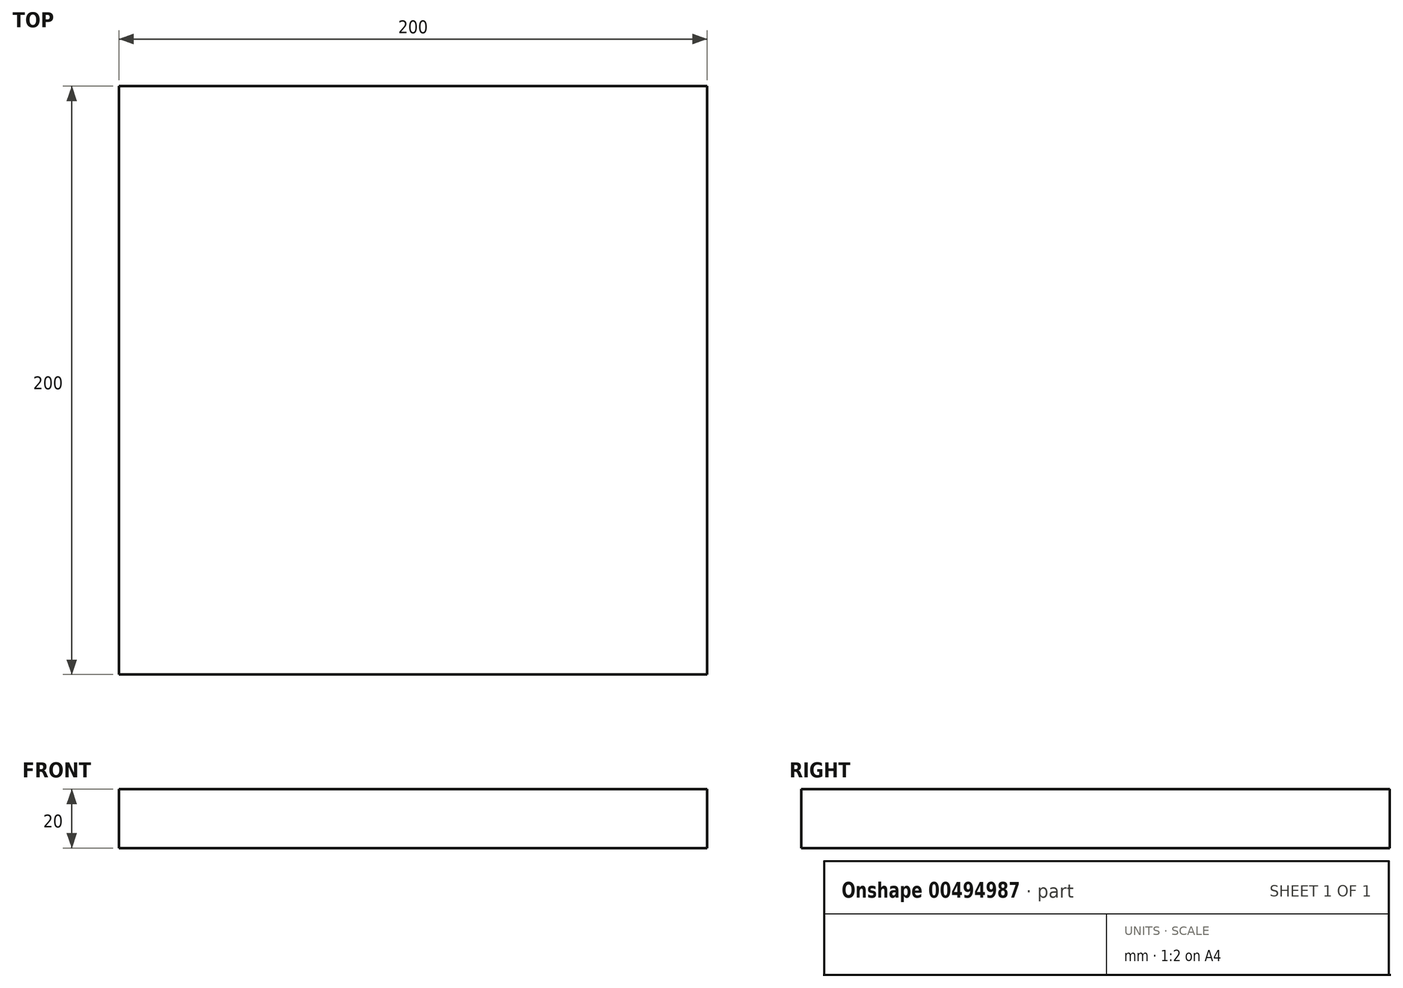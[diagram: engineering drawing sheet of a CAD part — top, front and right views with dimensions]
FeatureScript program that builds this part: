
annotation { "Feature Type Name" : "Feature", "Feature Type Description" : "" }
export const myFeature = defineFeature(function(context is Context, id is Id, definition is map)
    precondition{}
    {
        {
            var Q0;
            Q0=qCreatedBy(makeId("Top.planeOp"),FACE);
            var sketch = newSketch(context, id + "F0", { "sketchPlane" : qUnion([Q0])});
            skLineSegment(sketch, "E0.bottom", {"start": v(-200, 200) * mm, "end": v(0, 200) * mm});
            skLineSegment(sketch, "E0.top", {"start": v(-200, 0) * mm, "end": v(0, 0) * mm});
            skLineSegment(sketch, "E0.left", {"start": v(-200, 200) * mm, "end": v(-200, 0) * mm});
            skLineSegment(sketch, "E0.right", {"start": v(0, 200) * mm, "end": v(0, 0) * mm});
            skSolve(sketch);
        }
        {
            var Q0;
            Q0=qSketchRegion(id+"F0",true);
            extrude(context, id + "F1", {"entities" : qUnion([Q0]), "depth" : 20 * mm});
        }
    });
